# Revit family: 19320
name_source: partatom
category: Aparatos sanitarios
revit_build: Autodesk Revit 2018 (Build: 20170223_1515(x64)
units: mm (PartAtom-declared; Revit-internal decimal feet)

## family parameters
Anfitrión = Cara
Compartido = No
Corte con vacíos al cargar = No
Cota de conector redondo = Diámetro de uso
Número OmniClass = 23.45.55.14
Punto de cálculo de habitación = No
Tipo de pieza = Normal
Título OmniClass = Single Faucets

## types (1)
- 19320
    Accionamiento = Mediante pulsador
    CAUDAL = 1.5 l/min
    CIERRE = Automático en 7 seg.
    Comentarios de tipo = Cuerpo del fluxor en latón cromado, pieza interiores en materiales resistentes a la corrosión e incrustaciones calcáreas. Pistón/cabeza intercambiable que comprende todo el mecanismo del grifo. Dispositivo antisifónico que se asegura la protección de la red de agua potable contra las eventuales absorciones de agua contaminada. Caja de empotrar. Accionamiento de doble descarga con pulsador. Placa en acero inoxidable. Entrada macho 1". Caudal de 1,5 l/s. Cierra automático a los 7 ±2 s. Presión dinámica que necesita a la entrada el fluxor 1 bar. Salida para tubo de Ø28. Con llave de paso.
    Conexión AC = Sí
    Conexión AF = Sí
    Código de montaje = C1030220
    Descripción = Fluxor de fijación encastrado en el muro para inodoros, tazas turcas y vertederos.
    ENTRADA = Macho 1"
    Elevación por defecto = 1219 mm
    Fabricante = PRESTO IBÉRICA
    Imagen de tipo = <Ninguno>
    Material = Latón
    Modelo = PRESTO XT IE 2D Con llave de paso
    Presión Máxima = 8 bar
    REFERENCIA = 19320
    TIPO DE AGUA = Fria
    Teléfono = (+34) 915 782 575
    URL = http://www.griferiasgalindo.com
